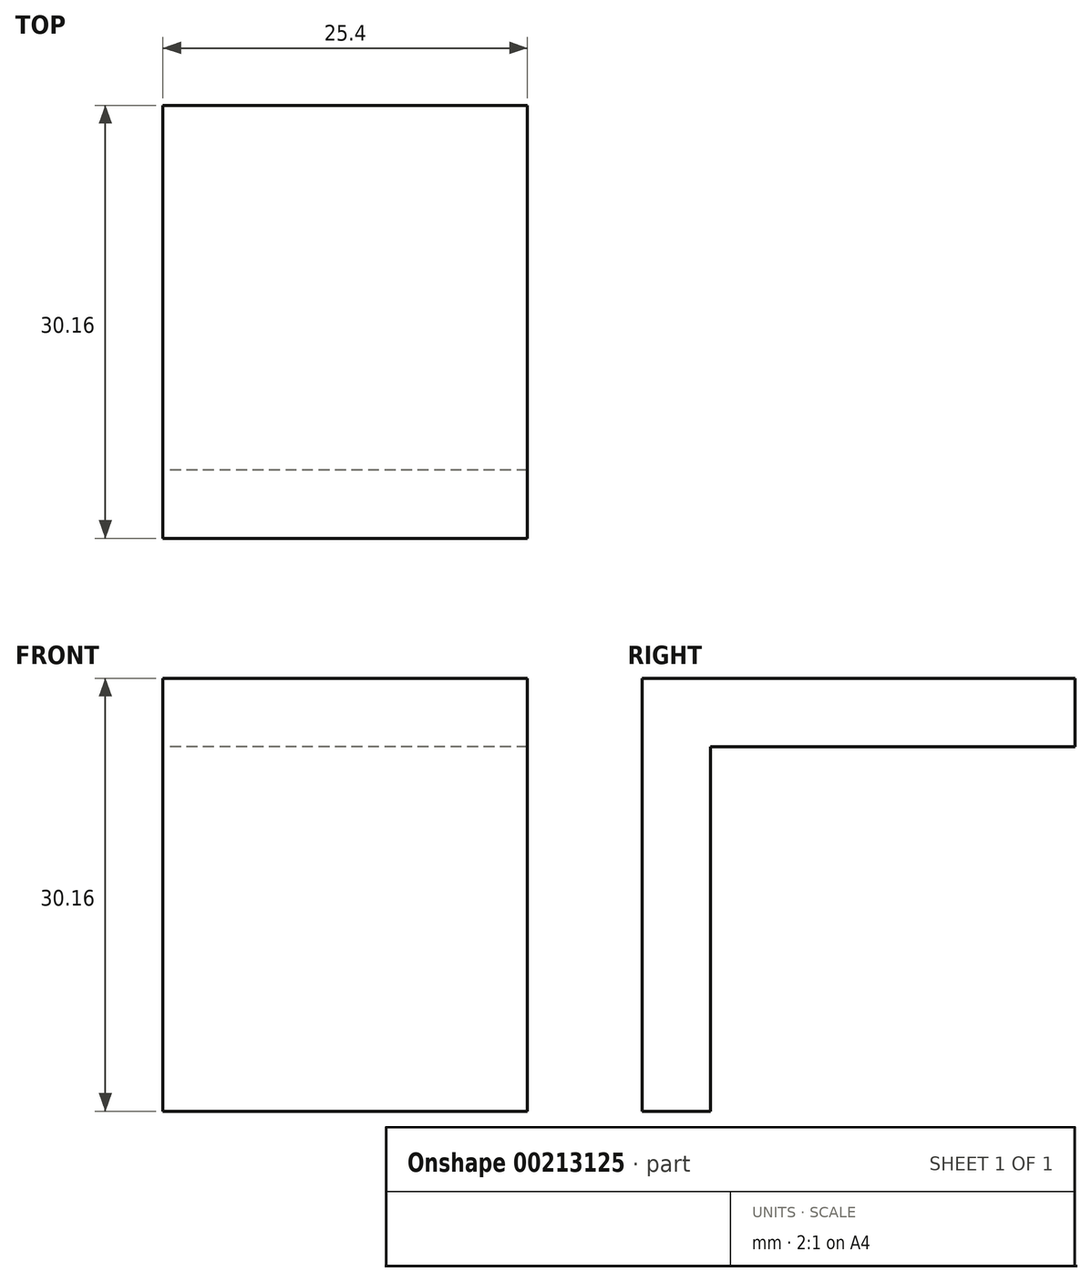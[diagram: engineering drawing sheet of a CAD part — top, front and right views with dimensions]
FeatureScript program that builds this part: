
annotation { "Feature Type Name" : "Feature", "Feature Type Description" : "" }
export const myFeature = defineFeature(function(context is Context, id is Id, definition is map)
    precondition{}
    {
        {
            var Q0;
            Q0=qCreatedBy(makeId("Right.planeOp"),FACE);
            var sketch = newSketch(context, id + "F0", { "sketchPlane" : qUnion([Q0])});
            skLineSegment(sketch, "E0.bottom", {"start": v(-12.7, 12.7) * mm, "end": v(12.7, 12.7) * mm});
            skLineSegment(sketch, "E0.left", {"start": v(-12.7, 12.7) * mm, "end": v(-12.7, -12.7) * mm});
            skPoint(sketch, "E0.middle", {"position": v(0, 0) * mm});
            skLineSegment(sketch, "E1.0", {"start": v(-17.46, 17.46) * mm, "end": v(-17.46, -12.7) * mm});
            skLineSegment(sketch, "E1.1", {"start": v(-17.46, 17.46) * mm, "end": v(12.7, 17.46) * mm});
            skLineSegment(sketch, "E2", {"start": v(-17.46, -12.7) * mm, "end": v(-12.7, -12.7) * mm});
            skLineSegment(sketch, "E3", {"start": v(12.7, 12.7) * mm, "end": v(12.7, 17.46) * mm});
            skPoint(sketch, "E0.top.end.orphan", {"position": v(12.7, -12.7) * mm});
            skSolve(sketch);
        }
        {
            var Q0;
            Q0=qSketchRegion(id+"F0",true);
            extrude(context, id + "F1", {"entities" : qUnion([Q0]), "endBound" : BoundingType.SYMMETRIC, "depth" : 25.4 * mm});
        }
    });
